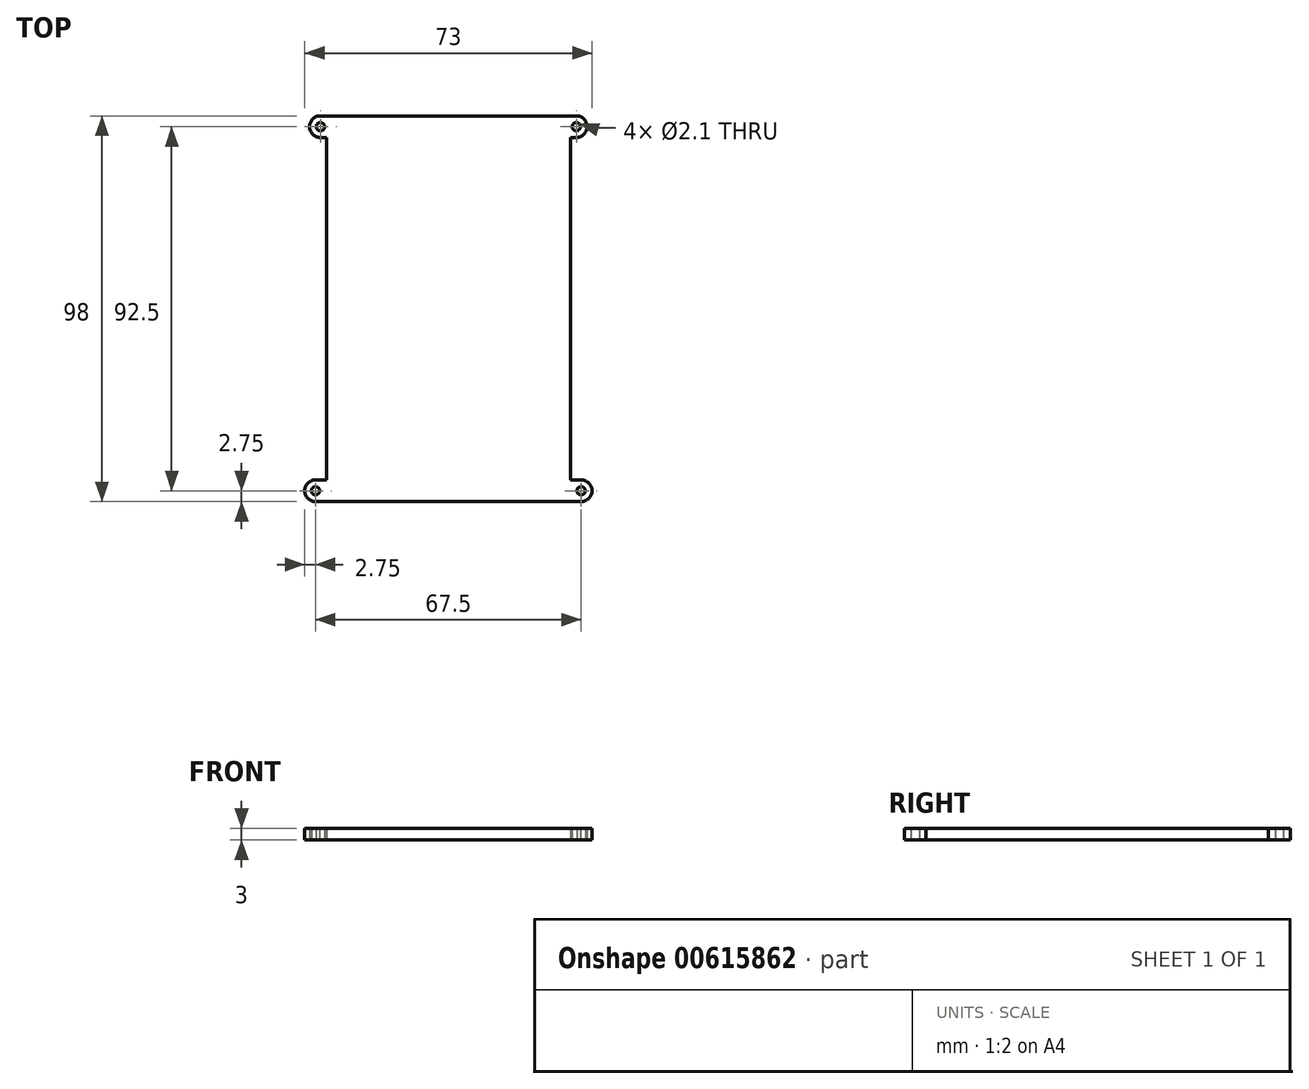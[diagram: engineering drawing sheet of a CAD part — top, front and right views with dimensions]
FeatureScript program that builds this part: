
annotation { "Feature Type Name" : "Feature", "Feature Type Description" : "" }
export const myFeature = defineFeature(function(context is Context, id is Id, definition is map)
    precondition{}
    {
        {
            var Q0;
            Q0=qCreatedBy(makeId("Top.planeOp"),FACE);
            var sketch = newSketch(context, id + "F0", { "sketchPlane" : qUnion([Q0])});
            skArc(sketch, "E0", {"start": v(-33.75, -43.5) * mm, "mid": v(-36.5, -46.25) * mm, "end": v(-33.75, -49) * mm});
            skLineSegment(sketch, "E1", {"start": v(33.75, -49) * mm, "end": v(-33.75, -49) * mm});
            skArc(sketch, "E2", {"start": v(33.75, -49) * mm, "mid": v(36.5, -46.25) * mm, "end": v(33.75, -43.5) * mm});
            skLineSegment(sketch, "E3", {"start": v(31, 43.5) * mm, "end": v(31, -43.5) * mm});
            skArc(sketch, "E4", {"start": v(32.5, 43.5) * mm, "mid": v(35.25, 46.25) * mm, "end": v(32.5, 49) * mm});
            skLineSegment(sketch, "E5", {"start": v(32.5, 49) * mm, "end": v(-32.5, 49) * mm});
            skArc(sketch, "E6", {"start": v(-32.5, 49) * mm, "mid": v(-35.25, 46.25) * mm, "end": v(-32.5, 43.5) * mm});
            skLineSegment(sketch, "E7", {"start": v(-31, 43.5) * mm, "end": v(-31, -43.5) * mm});
            skLineSegment(sketch, "E8", {"start": v(32.5, 43.5) * mm, "end": v(31, 43.5) * mm});
            skLineSegment(sketch, "E9", {"start": v(-31, 43.5) * mm, "end": v(-32.5, 43.5) * mm});
            skLineSegment(sketch, "E10", {"start": v(-31, -43.5) * mm, "end": v(-33.75, -43.5) * mm});
            skLineSegment(sketch, "E11", {"start": v(33.75, -43.5) * mm, "end": v(31, -43.5) * mm});
            skCircle(sketch, "E12", {"center": v(33.75, -46.25) * mm, "radius": 1.05 * mm});
            skCircle(sketch, "E13", {"center": v(-33.75, -46.25) * mm, "radius": 1.05 * mm});
            skCircle(sketch, "E14", {"center": v(-32.5, 46.25) * mm, "radius": 1.05 * mm});
            skCircle(sketch, "E15", {"center": v(32.5, 46.25) * mm, "radius": 1.05 * mm});
            skSolve(sketch);
        }
        {
            var Q0;
            Q0=makeQuery(id+"F0.imprint","IMPRINT",FACE,{"disambiguationData":[TD([[makeQuery(id+"F0.imprint","IMPRINT",EDGE,{"derivedFrom":sQuery(id+"F0.wireOp",EDGE,"E0")}),1.0]])]});
            extrude(context, id + "F1", {"entities" : qUnion([Q0]), "depth" : 3 * mm, "offsetDistance" : 25 * mm});
        }
    });
